# Revit family: Haworth_Very_Chair_SeminarStarBase_Visitor_EU_PRELIMINARY
name_source: partatom
category: Furniture
revit_build: Autodesk Revit 2018 (Build: 20170223_1515(x64)
units: mm (PartAtom-declared; Revit-internal decimal feet)

## family parameters
Always vertical = Yes
Cut with Voids When Loaded = No
OmniClass Number = 23.40.70.14.64.21
OmniClass Title = Systems Furniture
Room Calculation Point = No
Shared = No
Work Plane-Based = No

## types (6) — shared parameters
Actual Depth = 68 cm
Actual Height = 94 cm
Actual Width = 55 cm
Arm Cap Finish = Haworth _ Polymer _ Slate
Assembly Code = E2020200
Depth = 71 cm
Description = Haworth - Very - Chair - Seminar - Visitor
Manufacturer = Haworth
Model = 621X
Revision Number = 1
Size = Verify Final Dim. w/ Haworth
Sustainability Info = https://www.haworth.com
URL = https://www.haworth.com
URL - Product = https://www.haworth.com
Warranty = http://www.haworth.com

## per-type parameters (varying)
| type | Arms | Back Cushion | Caster Finish | Seat Cushion |
| without Arm, without Cushion | No | No | <By Category> | No |
| with Arm, without Cushion | Yes | No | <By Category> | No |
| without Arm, with both Cushion | No | Yes | <By Category> | Yes |
| with Arm, with both Cushion | Yes | Yes | Haworth - Plastic - Black | Yes |
| without Arm, with Seat Cushion | No | No | <By Category> | Yes |
| with Arm, with Seat Cushion | Yes | No | <By Category> | Yes |

## geometry (parser evidence)
native form markers: Blend x26, Sweep x10
no freeform markers — native parametric forms only
